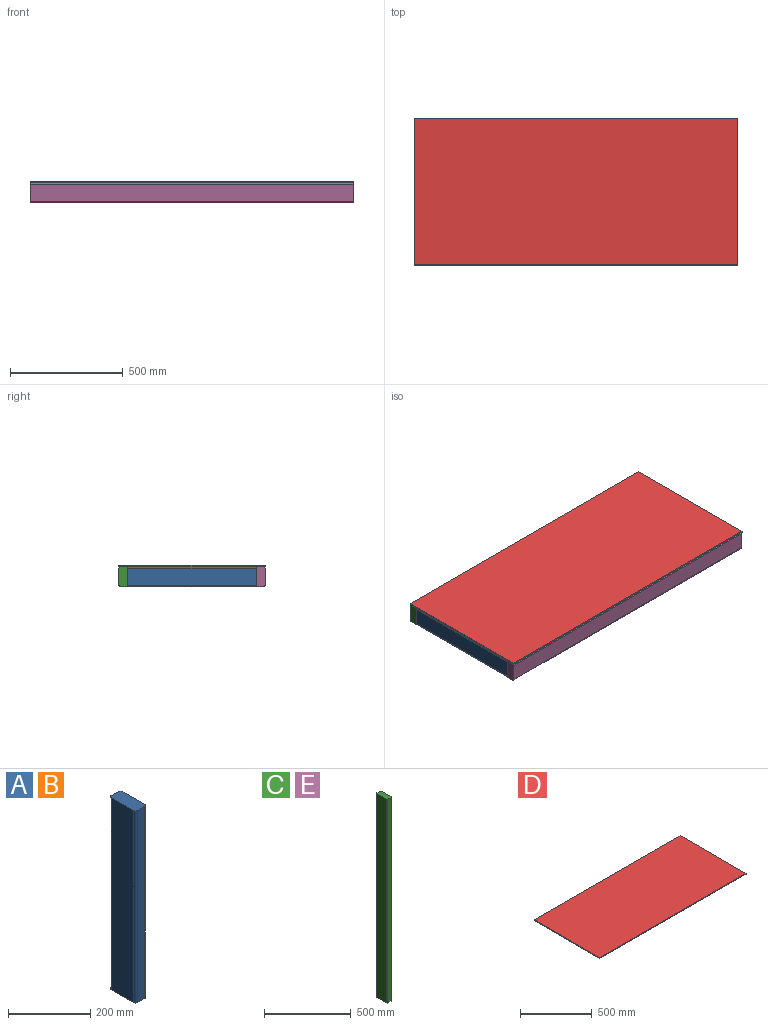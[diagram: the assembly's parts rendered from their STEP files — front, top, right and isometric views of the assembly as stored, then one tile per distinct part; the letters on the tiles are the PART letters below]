
ASSEMBLY  parts=5 mates=12
PART A: 10 faces, bbox 38.1x88.9x571.5 mm
  f0: plane 571.5x76.2mm, normal (-1,0,0), area 43548.3mm2, adj f1,f7,f8,f9
  f1: cylinder r=6.35mm len=571.5mm, axis (0,0,-1), area 5700.5mm2, adj f0,f2,f8,f9
  f2: plane 571.5x25.4mm, normal (0,-1,0), area 14516.1mm2, adj f1,f3,f8,f9
  f3: cylinder r=6.35mm len=571.5mm, axis (0,0,-1), area 5700.5mm2, adj f2,f4,f8,f9
  f4: plane 571.5x76.2mm, normal (1,0,0), area 43548.3mm2, adj f3,f5,f8,f9
  f5: cylinder r=6.35mm len=571.5mm, axis (0,0,-1), area 5700.5mm2, adj f4,f6,f8,f9
  f6: plane 571.5x25.4mm, normal (0,1,0), area 14516.1mm2, adj f5,f7,f8,f9
  f7: cylinder r=6.35mm len=571.5mm, axis (0,0,-1), area 5700.5mm2, adj f0,f6,f8,f9
  f8: plane 88.9x38.1mm, normal (0,0,1), area 3352.5mm2, adj f0,f1,f2,f3,f4,f5,f6,f7
  f9: plane 88.9x38.1mm, normal (0,0,-1), area 3352.5mm2, adj f0,f1,f2,f3,f4,f5,f6,f7
PART B: same geometry as A
PART C: 10 faces, bbox 38.1x88.9x1435.1 mm
  f0: plane 1435.1x76.2mm, normal (-1,0,0), area 109354.6mm2, adj f1,f7,f8,f9
  f1: cylinder r=6.35mm len=1435.1mm, axis (0,0,-1), area 14314.5mm2, adj f0,f2,f8,f9
  f2: plane 1435.1x25.4mm, normal (0,-1,0), area 36451.5mm2, adj f1,f3,f8,f9
  f3: cylinder r=6.35mm len=1435.1mm, axis (0,0,-1), area 14314.5mm2, adj f2,f4,f8,f9
  f4: plane 1435.1x76.2mm, normal (1,0,0), area 109354.6mm2, adj f3,f5,f8,f9
  f5: cylinder r=6.35mm len=1435.1mm, axis (0,0,-1), area 14314.5mm2, adj f4,f6,f8,f9
  f6: plane 1435.1x25.4mm, normal (0,1,0), area 36451.5mm2, adj f5,f7,f8,f9
  f7: cylinder r=6.35mm len=1435.1mm, axis (0,0,-1), area 14314.5mm2, adj f0,f6,f8,f9
  f8: plane 88.9x38.1mm, normal (0,0,1), area 3352.5mm2, adj f0,f1,f2,f3,f4,f5,f6,f7
  f9: plane 88.9x38.1mm, normal (0,0,-1), area 3352.5mm2, adj f0,f1,f2,f3,f4,f5,f6,f7
PART D: 6 faces, bbox 1435.1x647.7x6.4 mm
  f0: plane 1435.1x6.35mm, normal (0,1,0), area 9112.9mm2, adj f1,f3,f4,f5
  f1: plane 647.7x6.35mm, normal (-1,0,0), area 4112.9mm2, adj f0,f2,f4,f5
  f2: plane 1435.1x6.35mm, normal (0,-1,0), area 9112.9mm2, adj f1,f3,f4,f5
  f3: plane 647.7x6.35mm, normal (1,0,0), area 4112.9mm2, adj f0,f2,f4,f5
  f4: plane 1435.1x647.7mm, normal (0,0,1), area 929514.3mm2, adj f0,f1,f2,f3
  f5: plane 1435.1x647.7mm, normal (0,0,-1), area 929514.3mm2, adj f0,f1,f2,f3
PART E: same geometry as C
PLACE A rot(axis=(-1,0,0),90deg) t=(-1416.18,-323.85,-50.93)mm
PLACE B rot(axis=(0,0.71,0.71),180deg) t=(-18.92,-323.85,-50.67)mm
PLACE C rot(axis=(0.58,-0.58,-0.58),120deg) t=(-717.55,-19.44,-51.45)mm
PLACE D rot(axis=(-1,0,0),0deg) t=(-717.55,-323.85,-6.35)mm
PLACE E rot(axis=(-0.58,0.58,-0.58),120deg) t=(-717.55,-629.04,-50.15)mm
MATE planar E.f4 <-> D.f2  axis (0,-1,0) through (-717.55,-647.7,-50.8)mm
MATE planar B.f8 <-> C.f4  axis (0,1,0) through (-19.05,-38.1,-50.8)mm
MATE planar C.f0 <-> D.f0  axis (0,1,0) through (-717.55,0,-50.8)mm
MATE planar E.f9 <-> A.f0  axis (-1,0,0) through (-1435.1,-628.65,-50.8)mm
MATE planar D.f5 <-> A.f2  axis (0,0,-1) through (-717.55,-323.85,-6.35)mm
MATE planar E.f2 <-> D.f5  axis (0,0,1) through (-717.55,-628.65,-6.35)mm
MATE planar C.f8 <-> E.f9  axis (-1,0,0) through (-1435.1,-19.05,-50.8)mm
MATE planar E.f9 <-> D.f1  axis (-1,0,0) through (-1435.1,-628.65,-50.8)mm
MATE planar C.f6 <-> D.f5  axis (0,0,1) through (-717.55,-19.05,-6.35)mm
MATE planar A.f9 <-> E.f0  axis (0,-1,0) through (-1416.05,-609.6,-50.8)mm
MATE planar B.f6 <-> D.f5  axis (0,0,1) through (-19.05,-323.85,-6.35)mm
MATE planar B.f0 <-> C.f9  axis (1,0,0) through (0,-323.85,-50.8)mm
